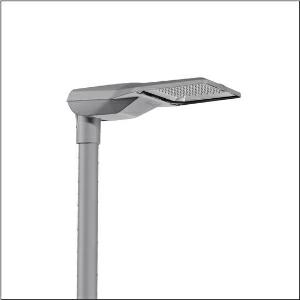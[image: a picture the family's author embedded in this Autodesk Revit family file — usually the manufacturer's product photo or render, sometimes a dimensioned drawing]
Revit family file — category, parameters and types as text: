
# Revit family: streetlight_sl_21_midi___st0_8a_5xe7c33a08mb_9d26
name_source: partatom
category: Lighting Fixtures
units: mm (PartAtom-declared; Revit-internal decimal feet)

## family parameters
Cut with Voids When Loaded = No
Host = Face
Light Source = No
Part Type = Normal
Room Calculation Point = No
Round Connector Dimension = Use Diameter
Shared = No

## types (1)
- --- (1 x LED, 18270 lm, 136 W, 3000K)
    Apparent Load = 136 VA
    CIE Flux Codes = 38 75 97 100 100
    Color Rendering = 70
    Color Temperature = 3000K
    Default Elevation = 1800 mm
    Description = Streetlight SL 21 midi, mast luminaire, primary light control with lens, of PMMA, primary optical cover: cover, of toughened safety glass, transparent, light distribution: ST0.8a, light emission: direct distribution, primary light characteristic: asymmetric, installation type: post-top, side-entry, LED, 3G 1.5mm², High Power LED, rated luminous flux: 18.270lm, luminous efficacy: 134lm/W, light colour: 730, colour temperature: 3000K, control: overheat protection, constant luminous flux control, time-dependent luminous flux control, flexible luminous flux parameterisation, mains connection: 220..240V, AC, 50/60Hz, connection cable pre-assembled, cable length: 12,5m, wiring characteristics: H07RN-F, start of lifetime: 136W, end of service life: 142W, reduction: 61W, luminaire housing, of diecast aluminium, powder-coated, Siteco® metallic grey (DB 702S), corrosivity category C5 mid according to DIN EN ISO 12944, please order mast flange separately, inclination adjustable: 0°, 5°, 10°, 15°, sealing non-destructively replaceable, multi-level sealing system, length: 644mm, width: 335mm, height: 110mm, mast flange for spigot size: 42mm (side-entry): 5XC10008XM4, 60/48mm (side-entry/post-top): 5XC10108XM2, 76/60mm (side-entry/post-top): 5XC10108XM1, protection rating (complete): IP66, insulation class (complete): insulation class II (safety insulation), certification: CE, ENEC, ENEC+, VDE, impact resistance: IK09, permissible operating ambient temperature for outdoor applications: -40..+50°C, standard-compliant lighting for roads and squares, packaging unit: 1 piece

Light Distribution: ST0.8a
    Height = 111 mm
    Lamp = 1 x LED
    Lamp Light Flux = 18270 lm
    Lamp Power = 136 W
    Lamp count = 1
    Length = 644 mm
    Luminous efficacy = 134 lm/W
    Manufacturer = Siteco
    ModVariant = No
    Model = 5XE7C33A08MB
    Number of Poles = 1
    OnlyDefault = Yes
    Power Factor = 1
    Product Name = Streetlight SL 21 midi | ST0.8a
    Product group = mast luminaire | pylon top
    ProductGroupID = 6100
    Protection Class = Protection class II
    Protection Degree = IP 66
    RLX_Detail_Level = 1
    RLX_Emergency_Light_Flux = 0 lm
    RLX_Emergency_Type = 0
    RLX_Emergency_Type_DB = No
    RlxData = <blob elided: 90621 chars, md5=db6b2b95>
    Socket = socket
    Standby Power = 0 W
    System Light Flux = 18270 lm
    System Power = 136 W
    Type Comments = factory setting: luminous flux: 100 % | Output Level: 100 % | 695 mA
    Type Image = l_1004298.jpg
    URL = http://relux.com
    VarID = @adj_157451
    Voltage = 0 V
    Weight = 0.00 kg
    Width = 336 mm

## geometry (parser evidence)
native form markers: Blend x4, Sweep x10
no freeform markers — native parametric forms only
